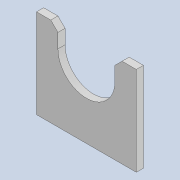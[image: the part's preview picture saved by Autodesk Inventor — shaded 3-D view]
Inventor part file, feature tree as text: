
AUTODESK INVENTOR PART (.ipt)
format: ipt  version: 2020 (Build 240168000, 168)  size: 92,672 bytes
history: native  units: mm
features: extrude x1, chamfer x1, sketch x1
ambient origin geometry x8: Origin, YZ Plane, XZ Plane, XY Plane, X Axis, Y Axis, Z Axis, Center Point
bodies: Solid1 (feature_tree)
feature tree (3):
  extrude  "Extrusion1"  Depth=25.0mm
  chamfer  "Chamfer2"  Distance=16.0mm
  sketch  "Sketch1"  dims[d0=28.0mm d1=25.0mm d2=16.0mm d4=11.0mm d5=2.0mm d6=0.0mm d10=2.0mm d11=2.0mm d12=45.0deg]
